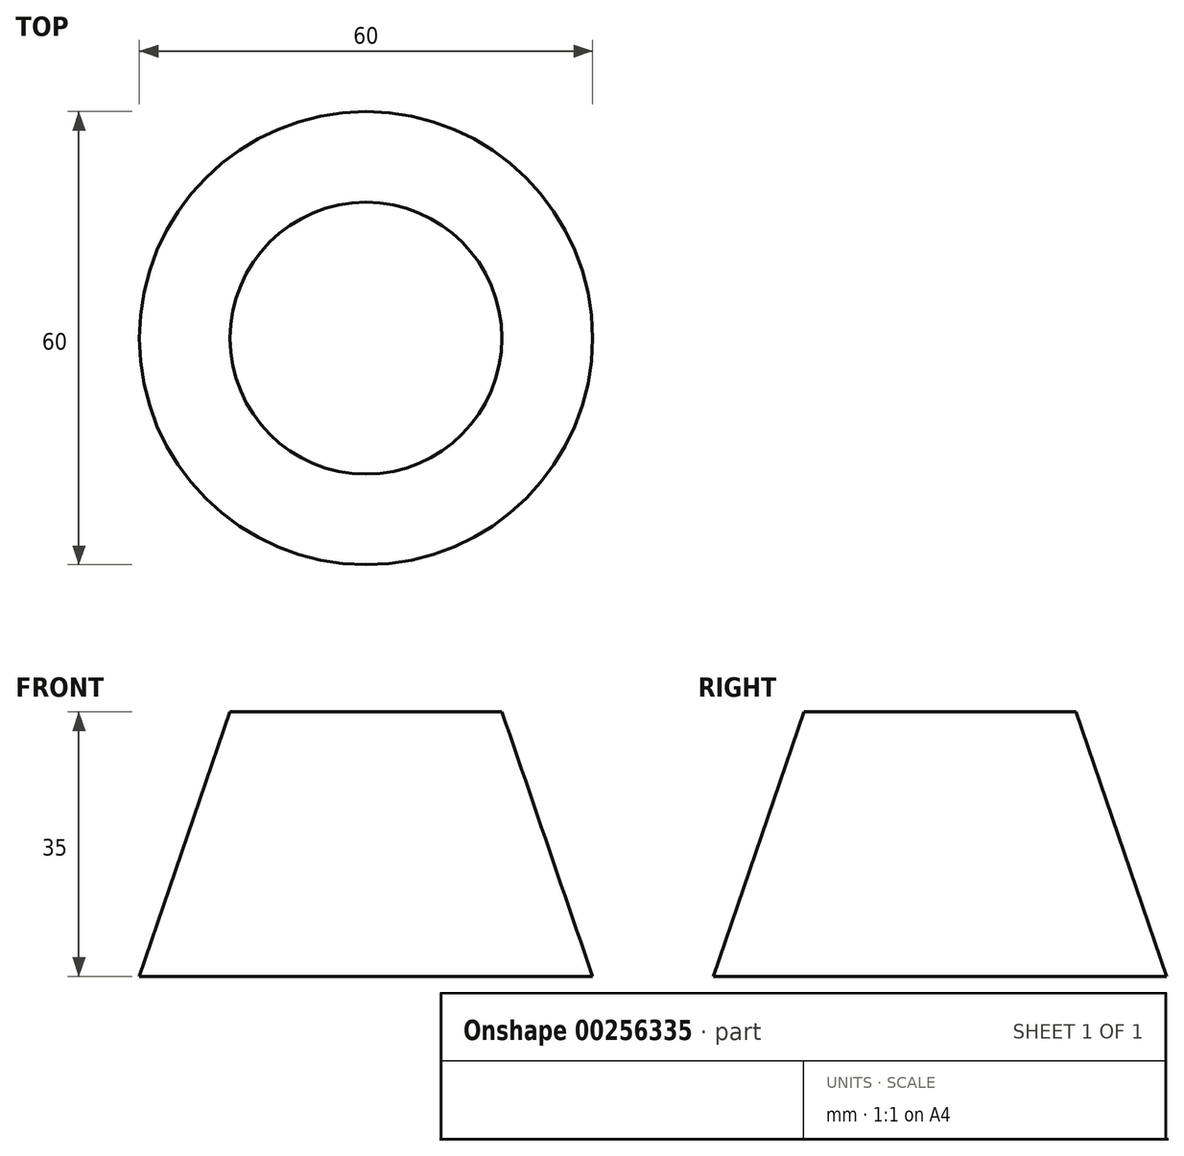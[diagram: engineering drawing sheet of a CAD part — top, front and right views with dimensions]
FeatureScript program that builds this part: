
annotation { "Feature Type Name" : "Feature", "Feature Type Description" : "" }
export const myFeature = defineFeature(function(context is Context, id is Id, definition is map)
    precondition{}
    {
        {
            var Q0;
            Q0=qCreatedBy(makeId("Front.planeOp"),FACE);
            var sketch = newSketch(context, id + "F0", { "sketchPlane" : qUnion([Q0])});
            skLineSegment(sketch, "E0", {"start": v(0, 0) * mm, "end": v(0, 35) * mm});
            skLineSegment(sketch, "E1", {"start": v(18, 35) * mm, "end": v(30, 0) * mm});
            skLineSegment(sketch, "E2", {"start": v(30, 0) * mm, "end": v(0, 0) * mm});
            skLineSegment(sketch, "E3", {"start": v(0, 35) * mm, "end": v(18, 35) * mm});
            skLineSegment(sketch, "E4", {"start": v(0, 63.26) * mm, "end": v(0, -53.22) * mm, "construction": true});
            skSolve(sketch);
        }
        {
            var Q0;
            Q0=makeQuery(id+"F0.imprint","IMPRINT",FACE,{"disambiguationData":[TD([[makeQuery(id+"F0.imprint","IMPRINT",EDGE,{"derivedFrom":sQuery(id+"F0.wireOp",EDGE,"E0")}),-1.0]])]});
            var Q1;
            Q1=sQuery(id+"F0.wireOp",EDGE,"E4");
            revolve(context, id + "F1", {"entities" : qUnion([Q0]), "axis" : qUnion([Q1]), "revolveType" : RevolveType.FULL});
        }
    });
